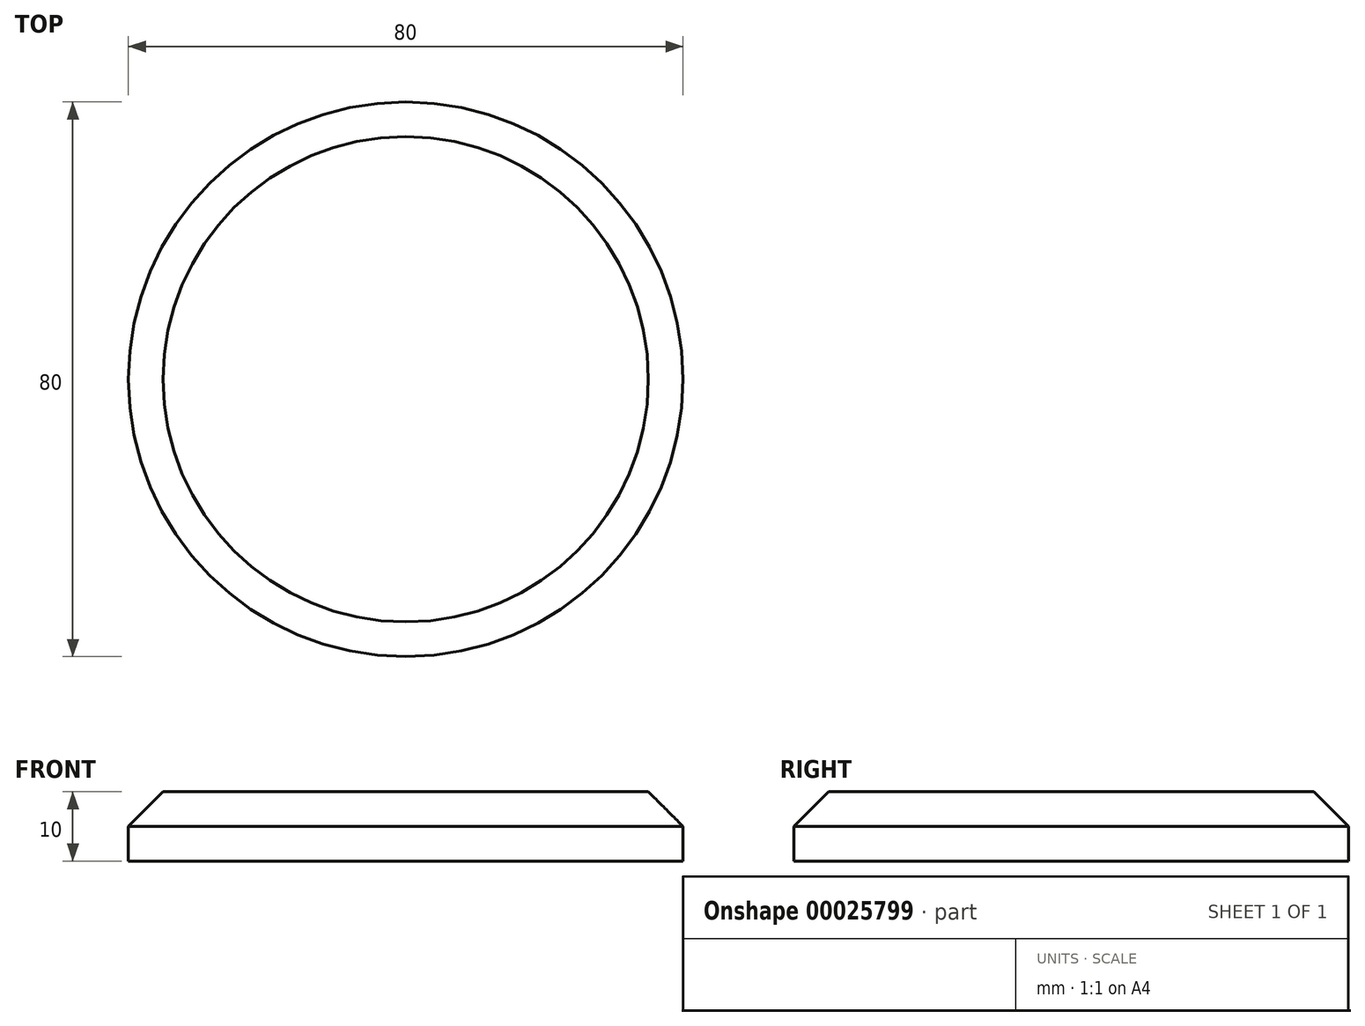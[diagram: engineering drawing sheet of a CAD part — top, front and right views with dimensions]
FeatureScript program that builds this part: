
annotation { "Feature Type Name" : "Feature", "Feature Type Description" : "" }
export const myFeature = defineFeature(function(context is Context, id is Id, definition is map)
    precondition{}
    {
        {
            var Q0;
            Q0=qCreatedBy(makeId("Top.planeOp"),FACE);
            var sketch = newSketch(context, id + "F0", { "sketchPlane" : qUnion([Q0])});
            skCircle(sketch, "E0", {"center": v(0, 0) * mm, "radius": 40 * mm});
            skSolve(sketch);
        }
        {
            var Q0;
            Q0=makeQuery(id+"F0.imprint","IMPRINT",FACE,{"disambiguationData":[TD([[makeQuery(id+"F0.imprint","IMPRINT",EDGE,{"derivedFrom":sQuery(id+"F0.wireOp",EDGE,"E0")}),1.0]])]});
            extrude(context, id + "F1", {"entities" : qUnion([Q0]), "depth" : 10 * mm});
        }
        {
            var Q0;
            Q0=makeQuery(id+"F1.opExtrude","CAP_EDGE",EDGE,{"disambiguationData":[OSD([sQuery(id+"F0.wireOp",EDGE,"E0")])],"isStart":false});
            chamfer(context, id + "F2", {"entities" : qUnion([Q0]), "width" : 5 * mm, "tangentPropagation" : true});
        }
    });
